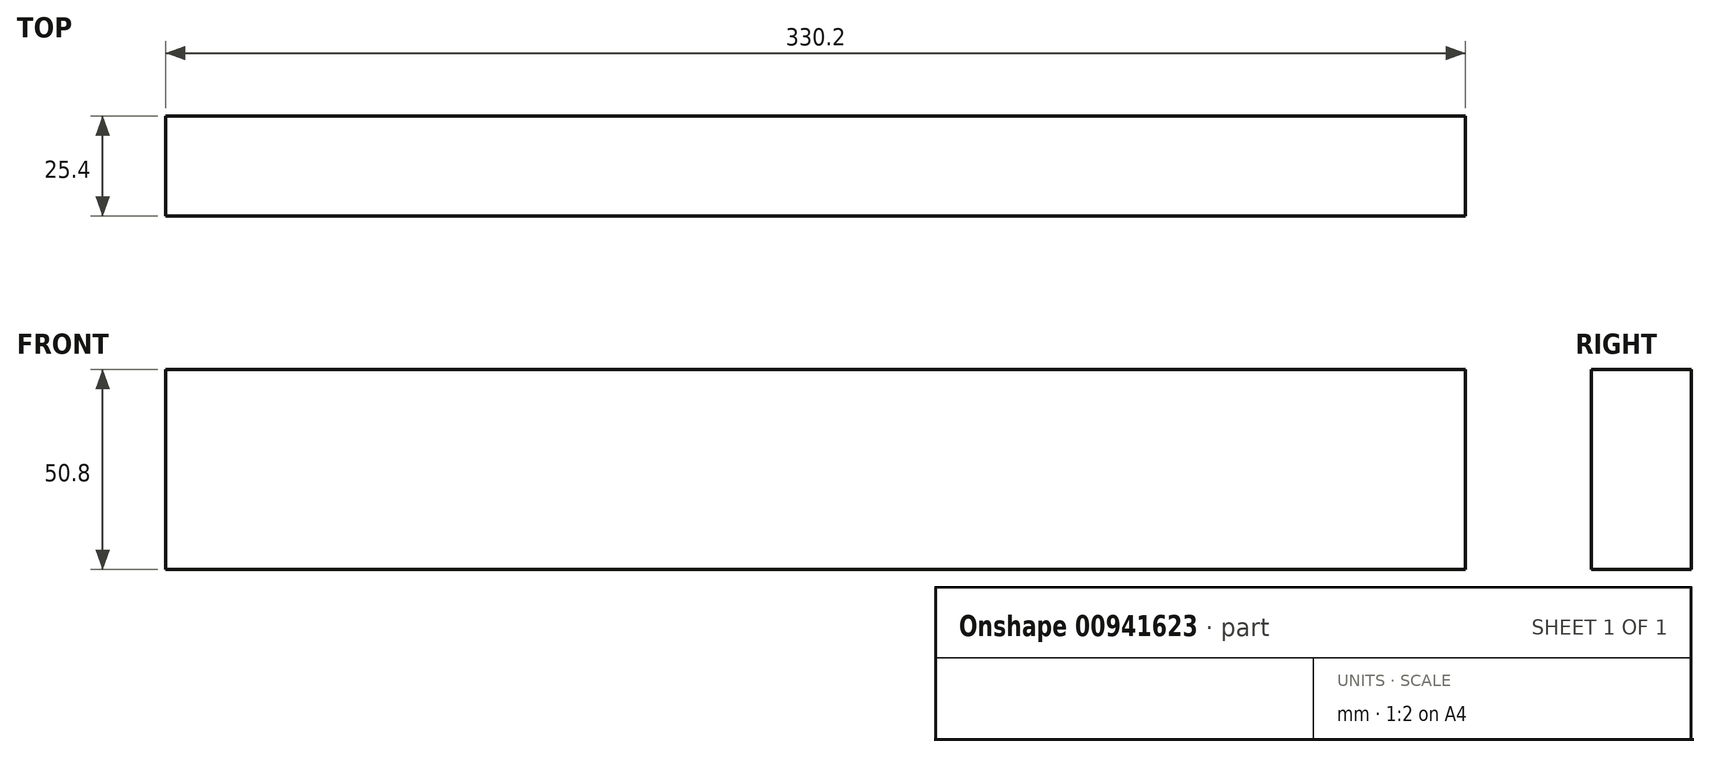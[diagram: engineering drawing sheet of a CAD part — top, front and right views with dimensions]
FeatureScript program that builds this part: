
annotation { "Feature Type Name" : "Feature", "Feature Type Description" : "" }
export const myFeature = defineFeature(function(context is Context, id is Id, definition is map)
    precondition{}
    {
        {
            var Q0;
            Q0=qCreatedBy(makeId("Front.planeOp"),FACE);
            var sketch = newSketch(context, id + "F0", { "sketchPlane" : qUnion([Q0])});
            skLineSegment(sketch, "E0.bottom", {"start": v(165.1, -25.4) * mm, "end": v(-165.1, -25.4) * mm});
            skLineSegment(sketch, "E0.top", {"start": v(165.1, 25.4) * mm, "end": v(-165.1, 25.4) * mm});
            skLineSegment(sketch, "E0.left", {"start": v(165.1, -25.4) * mm, "end": v(165.1, 25.4) * mm});
            skLineSegment(sketch, "E0.right", {"start": v(-165.1, -25.4) * mm, "end": v(-165.1, 25.4) * mm});
            skPoint(sketch, "E0.middle", {"position": v(0, 0) * mm});
            skSolve(sketch);
        }
        {
            var Q0;
            Q0=makeQuery(id+"F0.imprint","IMPRINT",FACE,{"disambiguationData":[TD([[makeQuery(id+"F0.imprint","IMPRINT",EDGE,{"derivedFrom":sQuery(id+"F0.wireOp",EDGE,"E0.bottom")}),-1.0]])]});
            extrude(context, id + "F1", {"entities" : qUnion([Q0]), "depth" : 25.4 * mm, "offsetDistance" : 25.4 * mm});
        }
    });
